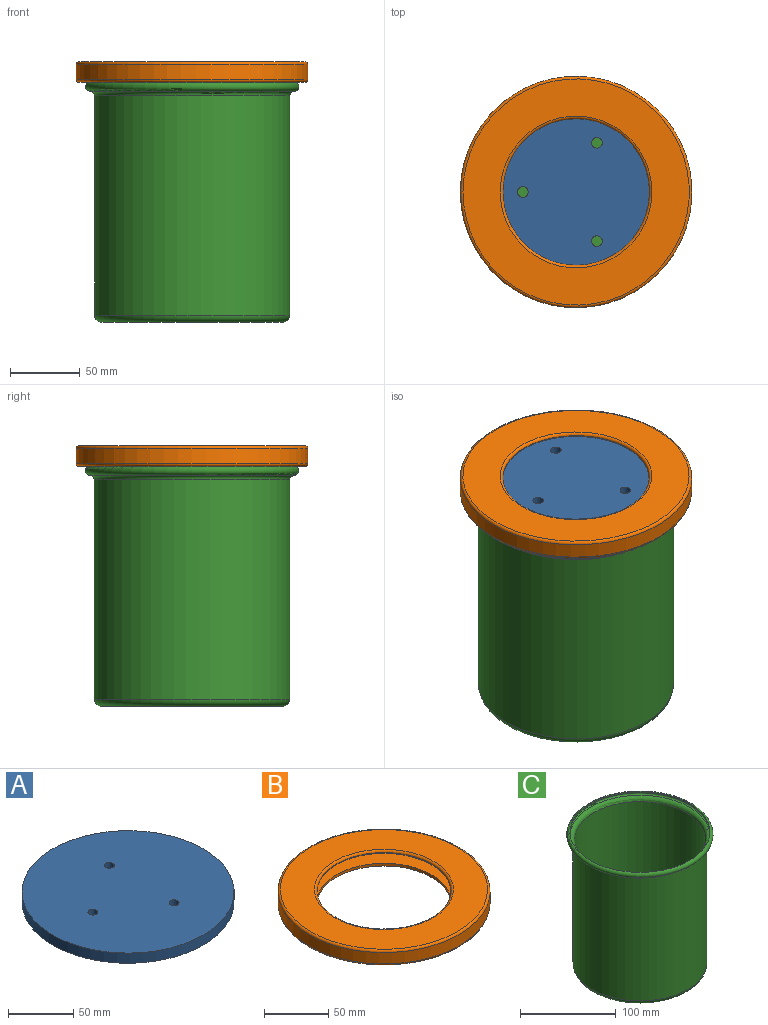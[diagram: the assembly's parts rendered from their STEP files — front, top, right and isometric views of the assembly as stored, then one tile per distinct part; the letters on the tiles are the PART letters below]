
ASSEMBLY  parts=3 mates=4
PART A: 6 faces, bbox 162.7x162.7x9.5 mm
  f0: cylinder r=81.35mm len=162.7mm, axis (0,0,-1), area 4868.7mm2, adj f1,f2
  f1: plane 162.7x162.7mm, normal (0,0,1), area 20654.9mm2, adj f0,f3,f4,f5
  f2: plane 162.7x162.7mm, normal (0,0,-1), area 20654.9mm2, adj f0,f3,f4,f5
  f3: cylinder r=3.81mm len=9.53mm, axis (0,0,1), area 228mm2, adj f1,f2
  f4: cylinder r=3.81mm len=9.53mm, axis (0,0,1), area 228mm2, adj f1,f2
  f5: cylinder r=3.81mm len=9.53mm, axis (0,0,1), area 228mm2, adj f1,f2
PART B: 11 faces, bbox 179.1x179.1x14.6 mm
  f0: cylinder r=52.31mm len=104.63mm, axis (0,0,-1), area 208.7mm2, adj f5,f8
  f1: plane 161.67x161.67mm, normal (0,0,1), area 11294.2mm2, adj f8,f10
  f2: cylinder r=52.31mm len=104.63mm, axis (0,0,-1), area 834.9mm2, adj f3,f7
  f3: plane 161.67x161.67mm, normal (0,0,-1), area 11931.8mm2, adj f2,f9
  f4: cylinder r=82.74mm len=165.48mm, axis (0,0,-1), area 5612.1mm2, adj f9,f10
  f5: plane 152.4x152.4mm, normal (0,0,-1), area 9643.6mm2, adj f0,f6
  f6: cylinder r=76.2mm len=152.4mm, axis (0,0,1), area 4560.3mm2, adj f5,f7
  f7: plane 152.4x152.4mm, normal (0,0,1), area 9643.6mm2, adj f2,f6
  f8: torus R=54.22mm, axis (0,0,-1), area 996.6mm2, adj f0,f1
  f9: torus R=80.84mm, axis (0,0,-1), area 1542.7mm2, adj f3,f4
  f10: torus R=80.84mm, axis (0,0,-1), area 1542.7mm2, adj f1,f4
PART C: 11 faces, bbox 165x165x171.5 mm
  f0: plane 129.54x129.54mm, normal (0,0,-1), area 13179.5mm2, adj f2
  f1: cylinder r=69.85mm len=156.85mm, axis (0,0,1), area 68836.2mm2, adj f2,f4
  f2: torus R=64.77mm, axis (0,0,1), area 3409.6mm2, adj f0,f1
  f3: torus R=73.03mm, axis (0,0,-1), area 4703.3mm2, adj f4,f5
  f4: torus R=73.03mm, axis (0,0,1), area 2225mm2, adj f1,f3
  f5: cylinder r=73.03mm len=146.05mm, axis (0,0,-1), area 728.4mm2, adj f3,f9
  f6: plane 129.54x129.54mm, normal (0,0,1), area 13179.5mm2, adj f8
  f7: cylinder r=68.26mm len=156.85mm, axis (0,0,1), area 67271.8mm2, adj f8,f10
  f8: torus R=64.77mm, axis (0,0,1), area 2309.2mm2, adj f6,f7
  f9: torus R=73.03mm, axis (0,0,-1), area 2320mm2, adj f5,f10
  f10: torus R=73.03mm, axis (0,0,1), area 3290mm2, adj f7,f9
PLACE A t=(0,0,-30.48)mm
PLACE B t=(0,0,-30.48)mm
PLACE C t=(0,0,-30.48)mm
MATE cylindrical B.f0 <-> C.f1  axis (0,0,-1) through (0,0,148.27)mm
MATE planar C.f1 <-> B.f0  axis (0,0,-1) through (0,0,140.97)mm
MATE planar A.f2 <-> B.f0  axis (0,0,-1) through (0.02,0,143.51)mm
MATE cylindrical A.f0 <-> C.f1  axis (0,0,-1) through (0,0,148.27)mm
